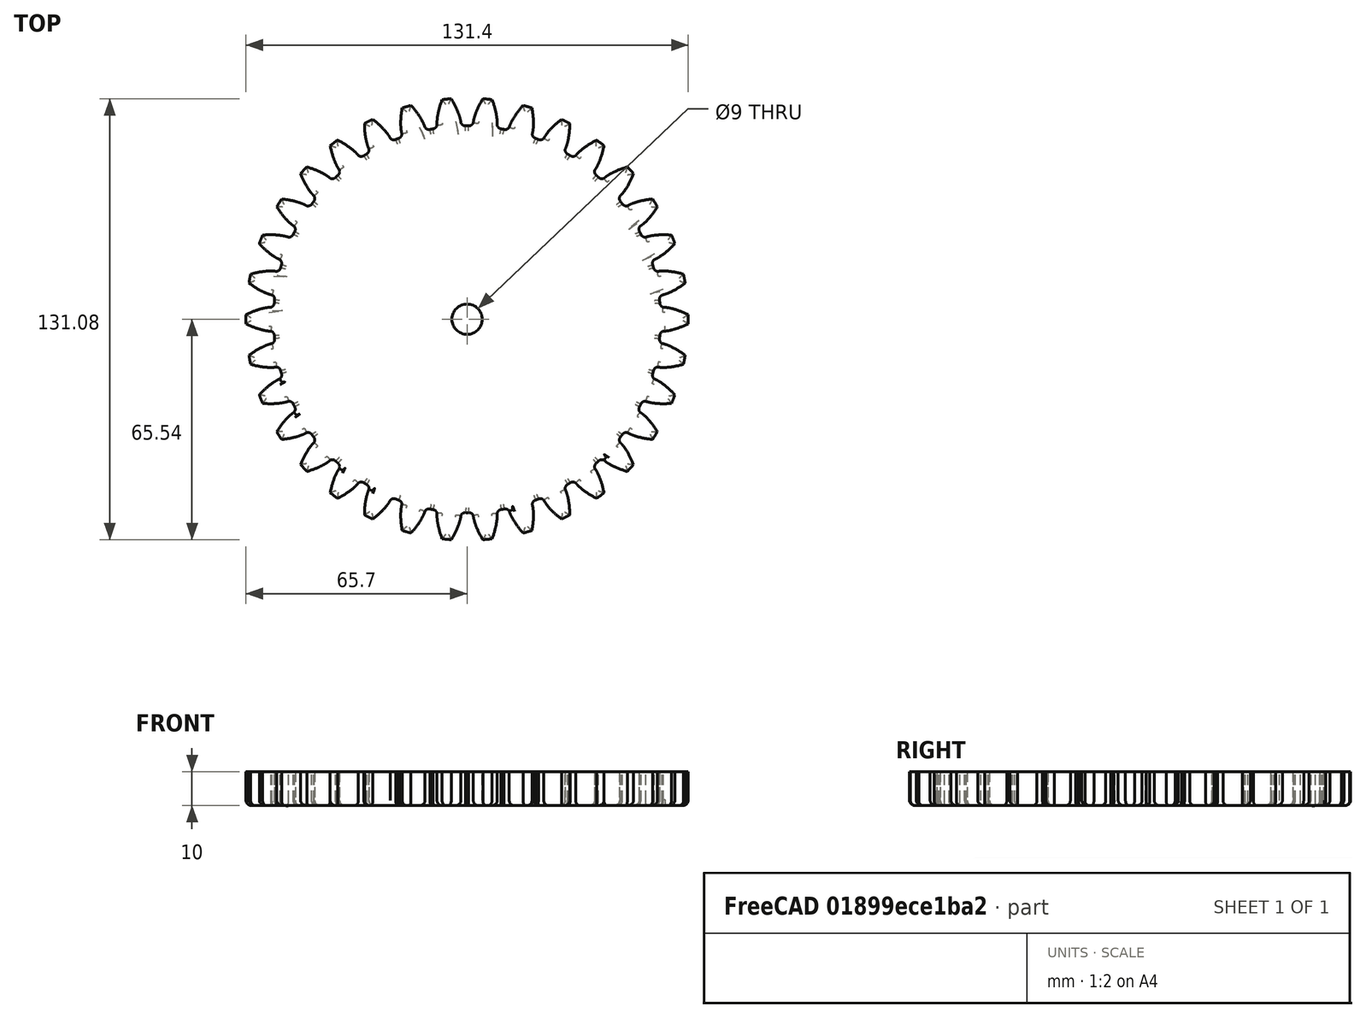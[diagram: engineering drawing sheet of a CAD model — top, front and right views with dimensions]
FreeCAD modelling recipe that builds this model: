
FCSTD DOCUMENT  (FreeCAD 0.16R6712 (Git))
Label: N34
License: All rights reserved
LicenseURL: http://en.wikipedia.org/wiki/All_rights_reserved
objects: Part::Cylinder×2, Part::Cut×2, Part::Part2DObjectPython×1, Part::Extrusion×1, Part::Fillet×1, Part::FeaturePython×1
note: 8 computed .brp shape members not serialized (recipe doc carries the construction recipe); baked Part::Feature solids carry a one-line shape summary decoded from their .brp

FEATURE [Part::Part2DObjectPython] InvoluteGear  # Draft 2D object (typed FeaturePython)
  ExternalGear = true
  HighPrecision = true
  MapMode = -1
  Modules = 3.65
  NumberOfTeeth = 34
  PressureAngle = 20
FEATURE [Part::Extrusion] Extrude001
  Base = -> InvoluteGear
  Dir = (0,0,1)
  Solid = true
FEATURE [Part::Cylinder] Cylinder  label="Cilindro"
  Angle = 360
  Height = 10
  Radius = 4.5
FEATURE [Part::Cut] Cut
  Base = -> Extrude001
  Tool = -> Cylinder
FEATURE [Part::Fillet] Fillet
  Base = -> Cut
  Edges = 273 edges r=1.5: [Edge3,Edge6,Edge9,Edge11,Edge12,Edge13,Edge14,Edge15,Edge16,Edge17,Edge18,Edge19,Edge20,Edge21,Edge22,Edge23,Edge24,Edge25,Edge26,Edge27,Edge28,Edge29,Edge30,Edge31,Edge32,Edge33,Edge34,Edge35,Edge36,Edge37,Edge38,Edge39,Edge40,Edge41,Edge42,Edge43,Edge44,Edge45,Edge46,Edge47,Edge48,Edge49,Edge50,+230 more]
FEATURE [Part::FeaturePython] Clone  label="Clone of ASROB_svg_30mm001"  # WARN: FeaturePython — macro-defined, semantics opaque (R4)
  Placement = pos=(-57,-38,12) rot=(0,0,1;0rad)
  Scale = (0.7,0.7,0.5)
FEATURE [Part::Cylinder] Cylinder001  label="Cilindro001"
  Angle = 360
  Height = 50
  Placement = pos=(0,0,-8) rot=(0,0,1;0rad)
  Radius = 4.5
FEATURE [Part::Cut] Cut001
  Base = -> Clone
  Tool = -> Cylinder001
